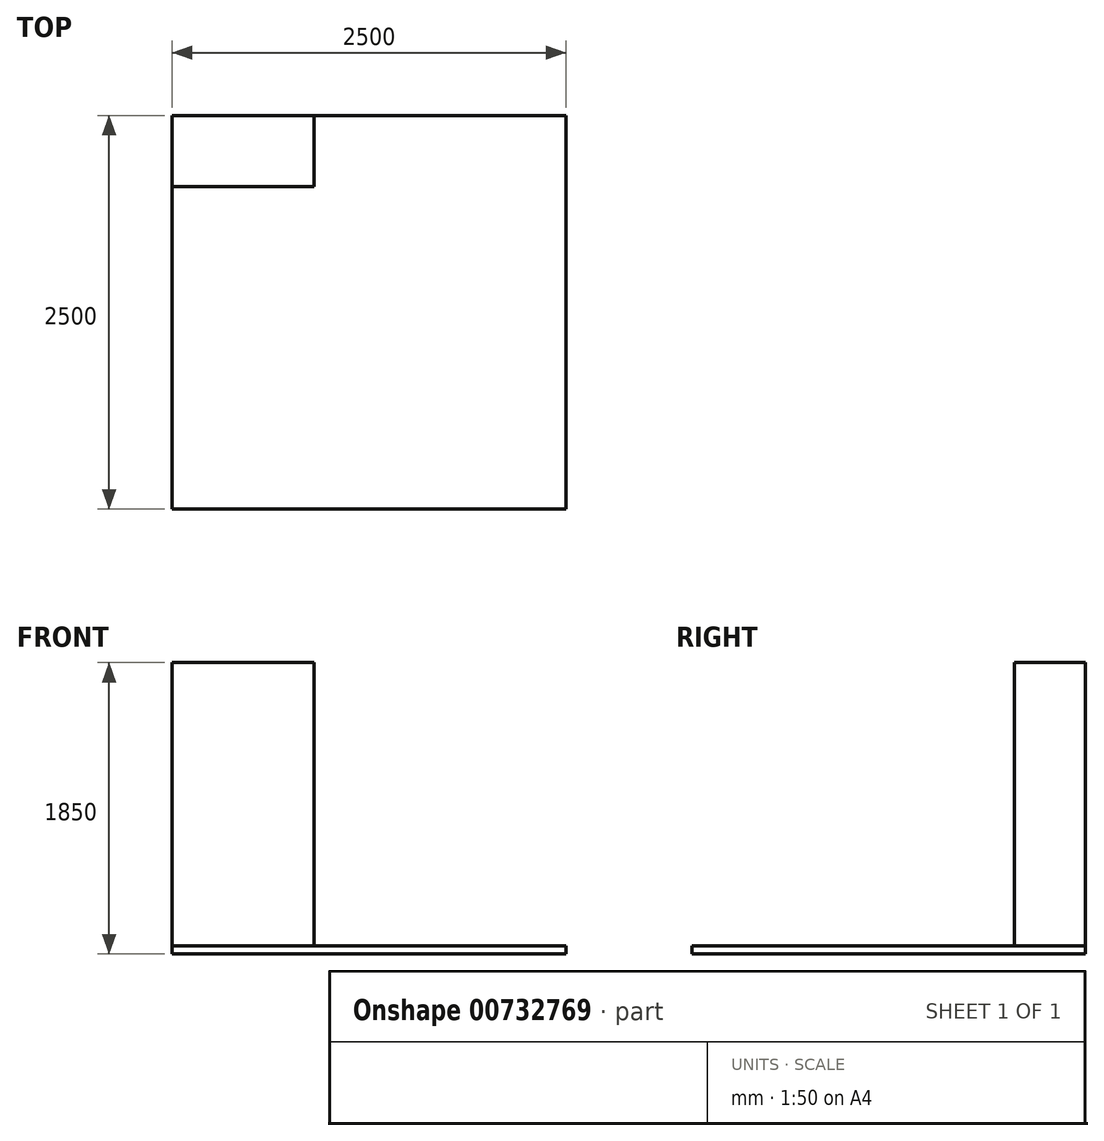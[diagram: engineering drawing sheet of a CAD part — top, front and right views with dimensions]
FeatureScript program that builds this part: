
annotation { "Feature Type Name" : "Feature", "Feature Type Description" : "" }
export const myFeature = defineFeature(function(context is Context, id is Id, definition is map)
    precondition{}
    {
        {
            var Q0;
            Q0=qCreatedBy(makeId("Top.planeOp"),FACE);
            var sketch = newSketch(context, id + "F0", { "sketchPlane" : qUnion([Q0])});
            skLineSegment(sketch, "E0.bottom", {"start": v(-1250, -1250) * mm, "end": v(1250, -1250) * mm});
            skLineSegment(sketch, "E0.top", {"start": v(-1250, 1250) * mm, "end": v(1250, 1250) * mm});
            skLineSegment(sketch, "E0.left", {"start": v(-1250, -1250) * mm, "end": v(-1250, 1250) * mm});
            skLineSegment(sketch, "E0.right", {"start": v(1250, -1250) * mm, "end": v(1250, 1250) * mm});
            skPoint(sketch, "E0.middle", {"position": v(0, 0) * mm});
            skSolve(sketch);
        }
        {
            var Q0;
            Q0=makeQuery(id+"F0.imprint","IMPRINT",FACE,{"disambiguationData":[TD([[makeQuery(id+"F0.imprint","IMPRINT",EDGE,{"derivedFrom":sQuery(id+"F0.wireOp",EDGE,"E0.bottom")}),1.0]])]});
            extrude(context, id + "F1", {"entities" : qUnion([Q0]), "oppositeDirection" : true, "depth" : 50 * mm, "offsetDistance" : 25 * mm});
        }
        {
            var Q0;
            Q0=makeQuery(id+"F1.opExtrude","CAP_FACE",FACE,{"disambiguationData":[OSD([sQuery(id+"F0.wireOp",EDGE,"E0.bottom"),sQuery(id+"F0.wireOp",EDGE,"E0.top"),sQuery(id+"F0.wireOp",EDGE,"E0.left"),sQuery(id+"F0.wireOp",EDGE,"E0.right")])],"isStart":true});
            var sketch = newSketch(context, id + "F2", { "sketchPlane" : qUnion([Q0])});
            skLineSegment(sketch, "E1.bottom", {"start": v(-1250, 1250) * mm, "end": v(-350, 1250) * mm});
            skLineSegment(sketch, "E1.top", {"start": v(-1250, 800) * mm, "end": v(-350, 800) * mm});
            skLineSegment(sketch, "E1.left", {"start": v(-1250, 1250) * mm, "end": v(-1250, 800) * mm});
            skLineSegment(sketch, "E1.right", {"start": v(-350, 1250) * mm, "end": v(-350, 800) * mm});
            skLineSegment(sketch, "E2.bottom", {"start": v(-300, 1250) * mm, "end": v(600, 1250) * mm});
            skLineSegment(sketch, "E2.top", {"start": v(-300, 800) * mm, "end": v(600, 800) * mm});
            skLineSegment(sketch, "E2.left", {"start": v(-300, 1250) * mm, "end": v(-300, 800) * mm});
            skLineSegment(sketch, "E2.right", {"start": v(600, 1250) * mm, "end": v(600, 800) * mm});
            skLineSegment(sketch, "E3.bottom", {"start": v(800, 750) * mm, "end": v(1250, 750) * mm});
            skLineSegment(sketch, "E3.top", {"start": v(800, -150) * mm, "end": v(1250, -150) * mm});
            skLineSegment(sketch, "E3.left", {"start": v(800, 750) * mm, "end": v(800, -150) * mm});
            skLineSegment(sketch, "E3.right", {"start": v(1250, 750) * mm, "end": v(1250, -150) * mm});
            skLineSegment(sketch, "E4.bottom", {"start": v(800, -200) * mm, "end": v(1250, -200) * mm});
            skLineSegment(sketch, "E4.top", {"start": v(800, -1100) * mm, "end": v(1250, -1100) * mm});
            skLineSegment(sketch, "E4.left", {"start": v(800, -200) * mm, "end": v(800, -1100) * mm});
            skLineSegment(sketch, "E4.right", {"start": v(1250, -200) * mm, "end": v(1250, -1100) * mm});
            skSolve(sketch);
        }
        {
            var Q0;
            Q0=makeQuery(id+"F2.imprint","IMPRINT",FACE,{"disambiguationData":[TD([[makeQuery(id+"F2.imprint","IMPRINT",EDGE,{"derivedFrom":sQuery(id+"F2.wireOp",EDGE,"E1.bottom")}),-1.0]])]});
            extrude(context, id + "F3", {"entities" : qUnion([Q0]), "operationType" : NewBodyOperationType.ADD, "depth" : 1800 * mm, "offsetDistance" : 25 * mm});
        }
    });
